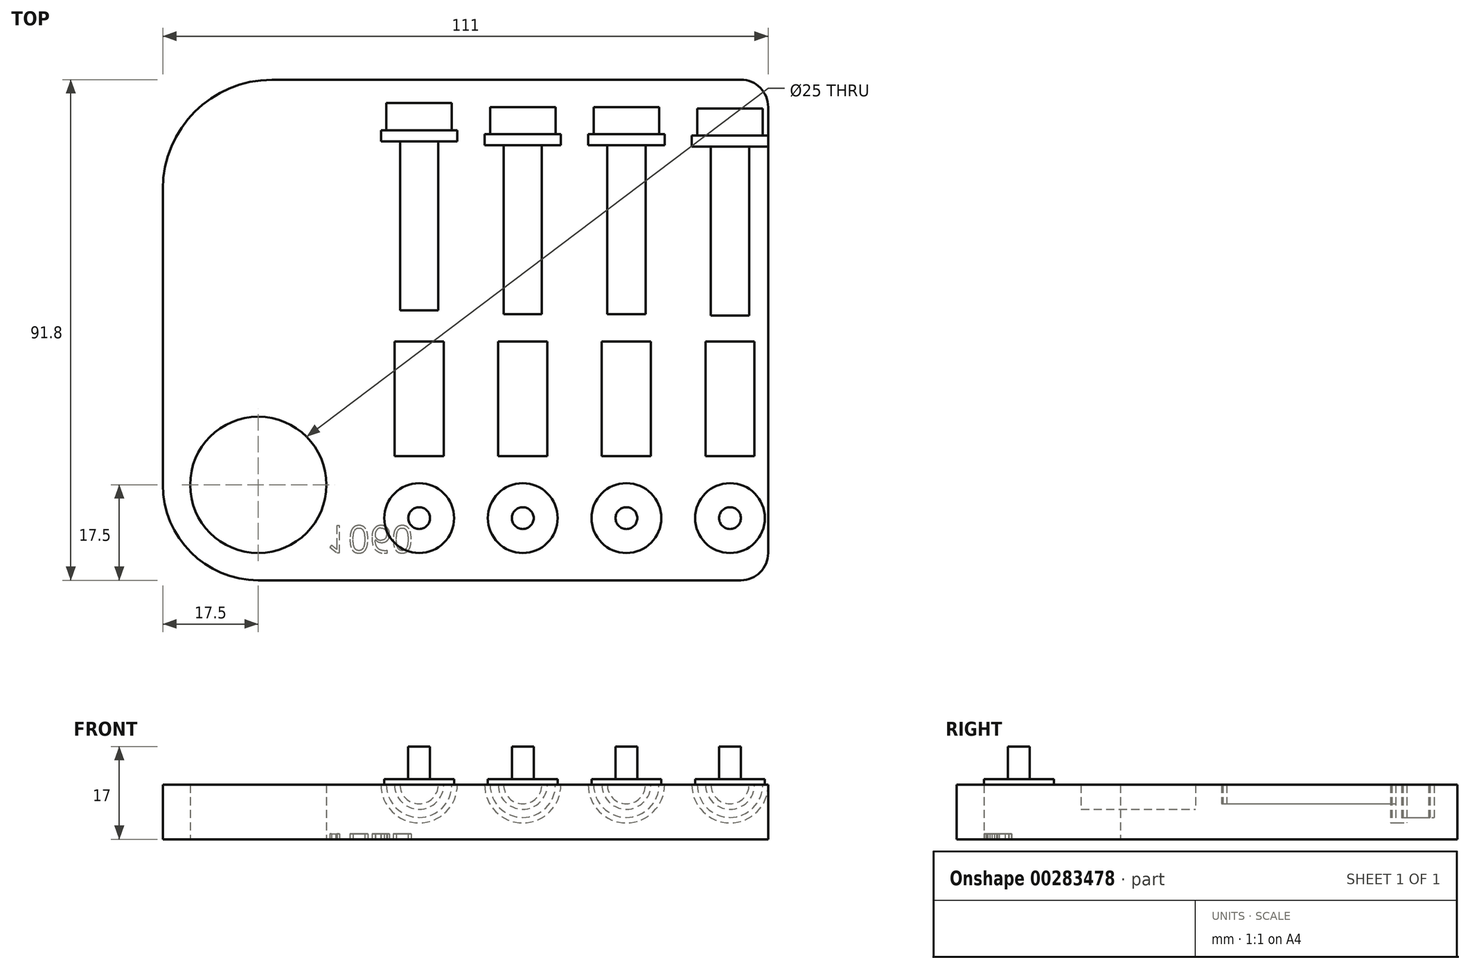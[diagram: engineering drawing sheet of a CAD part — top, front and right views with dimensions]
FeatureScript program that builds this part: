
annotation { "Feature Type Name" : "Feature", "Feature Type Description" : "" }
export const myFeature = defineFeature(function(context is Context, id is Id, definition is map)
    precondition{}
    {
        {
            var Q0;
            Q0=qCreatedBy(makeId("Top.planeOp"),FACE);
            var sketch = newSketch(context, id + "F0", { "sketchPlane" : qUnion([Q0])});
            skLineSegment(sketch, "E0.bottom", {"start": v(17.5, 0) * mm, "end": v(106, 0) * mm});
            skLineSegment(sketch, "E0.top", {"start": v(20, 91.8) * mm, "end": v(106, 91.8) * mm});
            skLineSegment(sketch, "E0.left", {"start": v(0, 17.5) * mm, "end": v(0, 71.8) * mm});
            skLineSegment(sketch, "E0.right", {"start": v(111, 5) * mm, "end": v(111, 86.8) * mm});
            skLineSegment(sketch, "E1.bottom", {"start": v(0, 0) * mm, "end": v(17.5, 0) * mm, "construction": true});
            skLineSegment(sketch, "E1.top", {"start": v(0, 17.5) * mm, "end": v(17.5, 17.5) * mm, "construction": true});
            skLineSegment(sketch, "E1.left", {"start": v(0, 0) * mm, "end": v(0, 17.5) * mm, "construction": true});
            skLineSegment(sketch, "E1.right", {"start": v(17.5, 0) * mm, "end": v(17.5, 17.5) * mm, "construction": true});
            skCircle(sketch, "E2", {"center": v(17.5, 17.5) * mm, "radius": 12.5 * mm});
            skPoint(sketch, "E3.visualSharp", {"position": v(0, 0) * mm});
            skArc(sketch, "E3.filletArc", {"start": v(0, 17.5) * mm, "mid": v(5.13, 5.13) * mm, "end": v(17.5, 0) * mm});
            skPoint(sketch, "E4.visualSharp", {"position": v(0, 91.8) * mm});
            skArc(sketch, "E4.filletArc", {"start": v(20, 91.8) * mm, "mid": v(5.86, 85.94) * mm, "end": v(0, 71.8) * mm});
            skPoint(sketch, "E5.visualSharp", {"position": v(111, 91.8) * mm});
            skArc(sketch, "E5.filletArc", {"start": v(111, 86.8) * mm, "mid": v(109.54, 90.34) * mm, "end": v(106, 91.8) * mm});
            skPoint(sketch, "E6.visualSharp", {"position": v(111, 0) * mm});
            skArc(sketch, "E6.filletArc", {"start": v(106, 0) * mm, "mid": v(109.54, 1.46) * mm, "end": v(111, 5) * mm});
            skSolve(sketch);
        }
        {
            var Q0;
            Q0=makeQuery(id+"F0.imprint","IMPRINT",FACE,{"disambiguationData":[TD([[makeQuery(id+"F0.imprint","IMPRINT",EDGE,{"derivedFrom":sQuery(id+"F0.wireOp",EDGE,"E0.bottom")}),1.0]])]});
            extrude(context, id + "F1", {"entities" : qUnion([Q0]), "depth" : 10 * mm});
        }
        {
            var Q0;
            Q0=makeQuery(id+"F1.opExtrude","CAP_FACE",FACE,{"disambiguationData":[OSD([sQuery(id+"F0.wireOp",EDGE,"E0.bottom"),sQuery(id+"F0.wireOp",EDGE,"E0.top"),sQuery(id+"F0.wireOp",EDGE,"E0.right"),sQuery(id+"F0.wireOp",EDGE,"E2"),sQuery(id+"F0.wireOp",EDGE,"E3.filletArc"),sQuery(id+"F0.wireOp",EDGE,"E4.filletArc"),sQuery(id+"F0.wireOp",EDGE,"E5.filletArc"),sQuery(id+"F0.wireOp",EDGE,"E6.filletArc")])],"isStart":false});
            var sketch = newSketch(context, id + "F2", { "sketchPlane" : qUnion([Q0])});
            skLineSegment(sketch, "E7.bottom", {"start": v(0, 0) * mm, "end": v(47, 0) * mm, "construction": true});
            skLineSegment(sketch, "E7.top", {"start": v(0, 11.4) * mm, "end": v(47, 11.4) * mm, "construction": true});
            skLineSegment(sketch, "E7.left", {"start": v(0, 0) * mm, "end": v(0, 11.4) * mm, "construction": true});
            skLineSegment(sketch, "E7.right", {"start": v(47, 0) * mm, "end": v(47, 11.4) * mm, "construction": true});
            skLineSegment(sketch, "E8.bottom", {"start": v(47, 11.4) * mm, "end": v(66, 11.4) * mm, "construction": true});
            skLineSegment(sketch, "E8.top", {"start": v(47, 22.8) * mm, "end": v(66, 22.8) * mm, "construction": true});
            skLineSegment(sketch, "E8.left", {"start": v(47, 11.4) * mm, "end": v(47, 22.8) * mm, "construction": true});
            skLineSegment(sketch, "E8.right", {"start": v(66, 11.4) * mm, "end": v(66, 22.8) * mm, "construction": true});
            skLineSegment(sketch, "E9.bottom", {"start": v(66, 11.4) * mm, "end": v(85, 11.4) * mm, "construction": true});
            skLineSegment(sketch, "E9.top", {"start": v(66, 22.8) * mm, "end": v(85, 22.8) * mm, "construction": true});
            skLineSegment(sketch, "E9.right", {"start": v(85, 11.4) * mm, "end": v(85, 22.8) * mm, "construction": true});
            skLineSegment(sketch, "E10.bottom", {"start": v(85, 11.4) * mm, "end": v(104, 11.4) * mm, "construction": true});
            skLineSegment(sketch, "E10.top", {"start": v(85, 22.8) * mm, "end": v(104, 22.8) * mm, "construction": true});
            skLineSegment(sketch, "E10.right", {"start": v(104, 11.4) * mm, "end": v(104, 22.8) * mm, "construction": true});
            skLineSegment(sketch, "E11.bottom", {"start": v(47, 22.8) * mm, "end": v(51.5, 22.8) * mm});
            skLineSegment(sketch, "E11.top", {"start": v(47, 43.8) * mm, "end": v(51.5, 43.8) * mm});
            skLineSegment(sketch, "E11.left", {"start": v(47, 22.8) * mm, "end": v(47, 43.8) * mm});
            skLineSegment(sketch, "E11.right", {"start": v(51.5, 22.8) * mm, "end": v(51.5, 43.8) * mm});
            skLineSegment(sketch, "E12.bottom", {"start": v(66, 22.8) * mm, "end": v(70.5, 22.8) * mm});
            skLineSegment(sketch, "E12.top", {"start": v(66, 43.8) * mm, "end": v(70.5, 43.8) * mm});
            skLineSegment(sketch, "E12.left", {"start": v(66, 22.8) * mm, "end": v(66, 43.8) * mm});
            skLineSegment(sketch, "E12.right", {"start": v(70.5, 22.8) * mm, "end": v(70.5, 43.8) * mm});
            skLineSegment(sketch, "E13.bottom", {"start": v(85, 22.8) * mm, "end": v(89.5, 22.8) * mm});
            skLineSegment(sketch, "E13.top", {"start": v(85, 43.8) * mm, "end": v(89.5, 43.8) * mm});
            skLineSegment(sketch, "E13.left", {"start": v(85, 22.8) * mm, "end": v(85, 43.8) * mm});
            skLineSegment(sketch, "E13.right", {"start": v(89.5, 22.8) * mm, "end": v(89.5, 43.8) * mm});
            skLineSegment(sketch, "E14.bottom", {"start": v(104, 22.8) * mm, "end": v(108.5, 22.8) * mm});
            skLineSegment(sketch, "E14.top", {"start": v(104, 43.8) * mm, "end": v(108.5, 43.8) * mm});
            skLineSegment(sketch, "E14.left", {"start": v(104, 22.8) * mm, "end": v(104, 43.8) * mm});
            skLineSegment(sketch, "E14.right", {"start": v(108.5, 22.8) * mm, "end": v(108.5, 43.8) * mm});
            skCircle(sketch, "E15", {"center": v(47, 11.4) * mm, "radius": 6.4 * mm});
            skCircle(sketch, "E16", {"center": v(66, 11.4) * mm, "radius": 6.4 * mm});
            skCircle(sketch, "E17", {"center": v(85, 11.4) * mm, "radius": 6.4 * mm});
            skCircle(sketch, "E18", {"center": v(104, 11.4) * mm, "radius": 6.4 * mm});
            skCircle(sketch, "E19", {"center": v(104, 11.4) * mm, "radius": 2 * mm});
            skCircle(sketch, "E20", {"center": v(85, 11.4) * mm, "radius": 2 * mm});
            skCircle(sketch, "E21", {"center": v(66, 11.4) * mm, "radius": 2 * mm});
            skCircle(sketch, "E22", {"center": v(47, 11.4) * mm, "radius": 2 * mm});
            skLineSegment(sketch, "E23", {"start": v(47, 43.8) * mm, "end": v(47, 48.8) * mm, "construction": true});
            skLineSegment(sketch, "E24", {"start": v(66, 43.8) * mm, "end": v(66, 48.8) * mm, "construction": true});
            skLineSegment(sketch, "E25", {"start": v(85, 43.8) * mm, "end": v(85, 48.8) * mm, "construction": true});
            skLineSegment(sketch, "E26", {"start": v(104, 43.8) * mm, "end": v(104, 48.55) * mm, "construction": true});
            skLineSegment(sketch, "E27.bottom", {"start": v(47, 49.52) * mm, "end": v(50.5, 49.52) * mm});
            skLineSegment(sketch, "E27.left", {"start": v(47, 49.52) * mm, "end": v(47, 80.52) * mm});
            skLineSegment(sketch, "E27.right", {"start": v(50.5, 49.52) * mm, "end": v(50.5, 80.52) * mm});
            skLineSegment(sketch, "E28.bottom", {"start": v(50.5, 80.52) * mm, "end": v(54, 80.52) * mm});
            skLineSegment(sketch, "E28.top", {"start": v(53, 82.52) * mm, "end": v(54, 82.52) * mm});
            skLineSegment(sketch, "E28.left", {"start": v(47, 80.52) * mm, "end": v(47, 82.52) * mm});
            skLineSegment(sketch, "E28.right", {"start": v(54, 80.52) * mm, "end": v(54, 82.52) * mm});
            skLineSegment(sketch, "E29.top", {"start": v(47, 87.52) * mm, "end": v(53, 87.52) * mm});
            skLineSegment(sketch, "E29.left", {"start": v(47, 82.52) * mm, "end": v(47, 87.52) * mm});
            skLineSegment(sketch, "E29.right", {"start": v(53, 82.52) * mm, "end": v(53, 87.52) * mm});
            skLineSegment(sketch, "E30.bottom", {"start": v(66, 48.8) * mm, "end": v(69.5, 48.8) * mm});
            skLineSegment(sketch, "E30.left", {"start": v(66, 48.8) * mm, "end": v(66, 79.8) * mm});
            skLineSegment(sketch, "E30.right", {"start": v(69.5, 48.8) * mm, "end": v(69.5, 79.8) * mm});
            skLineSegment(sketch, "E31.bottom", {"start": v(69.5, 79.8) * mm, "end": v(73, 79.8) * mm});
            skLineSegment(sketch, "E31.top", {"start": v(72, 81.8) * mm, "end": v(73, 81.8) * mm});
            skLineSegment(sketch, "E31.left", {"start": v(66, 79.8) * mm, "end": v(66, 81.8) * mm});
            skLineSegment(sketch, "E31.right", {"start": v(73, 79.8) * mm, "end": v(73, 81.8) * mm});
            skLineSegment(sketch, "E32.top", {"start": v(66, 86.8) * mm, "end": v(72, 86.8) * mm});
            skLineSegment(sketch, "E32.left", {"start": v(66, 81.8) * mm, "end": v(66, 86.8) * mm});
            skLineSegment(sketch, "E32.right", {"start": v(72, 81.8) * mm, "end": v(72, 86.8) * mm});
            skLineSegment(sketch, "E33.bottom", {"start": v(85, 48.8) * mm, "end": v(88.5, 48.8) * mm});
            skLineSegment(sketch, "E33.left", {"start": v(85, 48.8) * mm, "end": v(85, 79.8) * mm});
            skLineSegment(sketch, "E33.right", {"start": v(88.5, 48.8) * mm, "end": v(88.5, 79.8) * mm});
            skLineSegment(sketch, "E34.bottom", {"start": v(88.5, 79.8) * mm, "end": v(92, 79.8) * mm});
            skLineSegment(sketch, "E34.top", {"start": v(91, 81.8) * mm, "end": v(92, 81.8) * mm});
            skLineSegment(sketch, "E34.left", {"start": v(85, 79.8) * mm, "end": v(85, 81.8) * mm});
            skLineSegment(sketch, "E34.right", {"start": v(92, 79.8) * mm, "end": v(92, 81.8) * mm});
            skLineSegment(sketch, "E35.top", {"start": v(85, 86.8) * mm, "end": v(91, 86.8) * mm});
            skLineSegment(sketch, "E35.left", {"start": v(85, 81.8) * mm, "end": v(85, 86.8) * mm});
            skLineSegment(sketch, "E35.right", {"start": v(91, 81.8) * mm, "end": v(91, 86.8) * mm});
            skLineSegment(sketch, "E36.bottom", {"start": v(104, 48.55) * mm, "end": v(107.5, 48.55) * mm});
            skLineSegment(sketch, "E36.left", {"start": v(104, 48.55) * mm, "end": v(104, 79.55) * mm});
            skLineSegment(sketch, "E36.right", {"start": v(107.5, 48.55) * mm, "end": v(107.5, 79.55) * mm});
            skLineSegment(sketch, "E37.bottom", {"start": v(107.5, 79.55) * mm, "end": v(111, 79.55) * mm});
            skLineSegment(sketch, "E37.top", {"start": v(110, 81.55) * mm, "end": v(111, 81.55) * mm});
            skLineSegment(sketch, "E37.left", {"start": v(104, 79.55) * mm, "end": v(104, 81.55) * mm});
            skLineSegment(sketch, "E37.right", {"start": v(111, 79.55) * mm, "end": v(111, 81.55) * mm});
            skLineSegment(sketch, "E38.top", {"start": v(104, 86.55) * mm, "end": v(110, 86.55) * mm});
            skLineSegment(sketch, "E38.left", {"start": v(104, 81.55) * mm, "end": v(104, 86.55) * mm});
            skLineSegment(sketch, "E38.right", {"start": v(110, 81.55) * mm, "end": v(110, 86.55) * mm});
            skSolve(sketch);
        }
        {
            var Q0;
            Q0=makeQuery(id+"F2.imprint","IMPRINT",FACE,{"disambiguationData":[TD([[makeQuery(id+"F2.imprint","IMPRINT",EDGE,{"derivedFrom":sQuery(id+"F2.wireOp",EDGE,"E27.bottom")}),1.0]])]});
            var Q1;
            Q1=makeQuery(id+"F2.imprint","IMPRINT",FACE,{"disambiguationData":[TD([[makeQuery(id+"F2.imprint","IMPRINT",EDGE,{"derivedFrom":sQuery(id+"F2.wireOp",EDGE,"E11.bottom")}),1.0]])]});
            var Q2;
            Q2=sQuery(id+"F2.wireOp",EDGE,"E11.left");
            revolve(context, id + "F3", {"operationType" : NewBodyOperationType.REMOVE, "entities" : qUnion([Q0, Q1]), "axis" : qUnion([Q2]), "revolveType" : RevolveType.FULL, "oppositeDirection" : true});
        }
        {
            var Q0;
            Q0=makeQuery(id+"F2.imprint","IMPRINT",FACE,{"disambiguationData":[TD([[makeQuery(id+"F2.imprint","IMPRINT",EDGE,{"derivedFrom":sQuery(id+"F2.wireOp",EDGE,"E30.bottom")}),1.0]])]});
            var Q1;
            Q1=makeQuery(id+"F2.imprint","IMPRINT",FACE,{"disambiguationData":[TD([[makeQuery(id+"F2.imprint","IMPRINT",EDGE,{"derivedFrom":sQuery(id+"F2.wireOp",EDGE,"E12.bottom")}),1.0]])]});
            var Q2;
            Q2=sQuery(id+"F2.wireOp",EDGE,"E12.left");
            revolve(context, id + "F4", {"operationType" : NewBodyOperationType.REMOVE, "entities" : qUnion([Q0, Q1]), "axis" : qUnion([Q2]), "revolveType" : RevolveType.FULL, "oppositeDirection" : true});
        }
        {
            var Q0;
            Q0=makeQuery(id+"F2.imprint","IMPRINT",FACE,{"disambiguationData":[TD([[makeQuery(id+"F2.imprint","IMPRINT",EDGE,{"derivedFrom":sQuery(id+"F2.wireOp",EDGE,"E33.bottom")}),1.0]])]});
            var Q1;
            Q1=makeQuery(id+"F2.imprint","IMPRINT",FACE,{"disambiguationData":[TD([[makeQuery(id+"F2.imprint","IMPRINT",EDGE,{"derivedFrom":sQuery(id+"F2.wireOp",EDGE,"E13.bottom")}),1.0]])]});
            var Q2;
            Q2=sQuery(id+"F2.wireOp",EDGE,"E13.left");
            revolve(context, id + "F5", {"operationType" : NewBodyOperationType.REMOVE, "entities" : qUnion([Q0, Q1]), "axis" : qUnion([Q2]), "revolveType" : RevolveType.FULL, "oppositeDirection" : true});
        }
        {
            var Q0;
            Q0=makeQuery(id+"F2.imprint","IMPRINT",FACE,{"disambiguationData":[TD([[makeQuery(id+"F2.imprint","IMPRINT",EDGE,{"derivedFrom":sQuery(id+"F2.wireOp",EDGE,"E36.bottom")}),1.0]])]});
            var Q1;
            Q1=makeQuery(id+"F2.imprint","IMPRINT",FACE,{"disambiguationData":[TD([[makeQuery(id+"F2.imprint","IMPRINT",EDGE,{"derivedFrom":sQuery(id+"F2.wireOp",EDGE,"E14.bottom")}),1.0]])]});
            var Q2;
            Q2=sQuery(id+"F2.wireOp",EDGE,"E36.left");
            revolve(context, id + "F6", {"operationType" : NewBodyOperationType.REMOVE, "entities" : qUnion([Q0, Q1]), "axis" : qUnion([Q2]), "revolveType" : RevolveType.FULL, "oppositeDirection" : true});
        }
        {
            var Q0;
            Q0=makeQuery(id+"F2.imprint","IMPRINT",FACE,{"disambiguationData":[TD([[makeQuery(id+"F2.imprint","IMPRINT",EDGE,{"derivedFrom":sQuery(id+"F2.wireOp",EDGE,"E15")}),1.0]])]});
            var Q1;
            Q1=makeQuery(id+"F2.imprint","IMPRINT",FACE,{"disambiguationData":[TD([[makeQuery(id+"F2.imprint","IMPRINT",EDGE,{"derivedFrom":sQuery(id+"F2.wireOp",EDGE,"E16")}),1.0]])]});
            var Q2;
            Q2=makeQuery(id+"F2.imprint","IMPRINT",FACE,{"disambiguationData":[TD([[makeQuery(id+"F2.imprint","IMPRINT",EDGE,{"derivedFrom":sQuery(id+"F2.wireOp",EDGE,"E17")}),1.0]])]});
            var Q3;
            Q3=makeQuery(id+"F2.imprint","IMPRINT",FACE,{"disambiguationData":[TD([[makeQuery(id+"F2.imprint","IMPRINT",EDGE,{"derivedFrom":sQuery(id+"F2.wireOp",EDGE,"E18")}),1.0]])]});
            extrude(context, id + "F7", {"entities" : qUnion([Q0, Q1, Q2, Q3]), "operationType" : NewBodyOperationType.ADD, "depth" : 1 * mm});
        }
        {
            var Q0;
            Q0=makeQuery(id+"F2.imprint","IMPRINT",FACE,{"disambiguationData":[TD([[makeQuery(id+"F2.imprint","IMPRINT",EDGE,{"derivedFrom":sQuery(id+"F2.wireOp",EDGE,"E21")}),1.0]])]});
            var Q1;
            Q1=makeQuery(id+"F2.imprint","IMPRINT",FACE,{"disambiguationData":[TD([[makeQuery(id+"F2.imprint","IMPRINT",EDGE,{"derivedFrom":sQuery(id+"F2.wireOp",EDGE,"E22")}),1.0]])]});
            var Q2;
            Q2=makeQuery(id+"F2.imprint","IMPRINT",FACE,{"disambiguationData":[TD([[makeQuery(id+"F2.imprint","IMPRINT",EDGE,{"derivedFrom":sQuery(id+"F2.wireOp",EDGE,"E20")}),1.0]])]});
            var Q3;
            Q3=makeQuery(id+"F2.imprint","IMPRINT",FACE,{"disambiguationData":[TD([[makeQuery(id+"F2.imprint","IMPRINT",EDGE,{"derivedFrom":sQuery(id+"F2.wireOp",EDGE,"E19")}),1.0]])]});
            extrude(context, id + "F8", {"entities" : qUnion([Q0, Q1, Q2, Q3]), "operationType" : NewBodyOperationType.ADD, "depth" : 7 * mm});
        }
        {
            var Q0;
            Q0=makeQuery(id+"F1.opExtrude","CAP_FACE",FACE,{"disambiguationData":[OSD([sQuery(id+"F0.wireOp",EDGE,"E0.bottom"),sQuery(id+"F0.wireOp",EDGE,"E0.top"),sQuery(id+"F0.wireOp",EDGE,"E0.left"),sQuery(id+"F0.wireOp",EDGE,"E0.right"),sQuery(id+"F0.wireOp",EDGE,"E2"),sQuery(id+"F0.wireOp",EDGE,"E3.filletArc"),sQuery(id+"F0.wireOp",EDGE,"E4.filletArc"),sQuery(id+"F0.wireOp",EDGE,"E5.filletArc"),sQuery(id+"F0.wireOp",EDGE,"E6.filletArc")])],"isStart":true});
            var sketch = newSketch(context, id + "F9", { "sketchPlane" : qUnion([Q0])});
            skLineSegment(sketch, "E39.bottom", {"start": v(0, 0) * mm, "end": v(30, 0) * mm, "construction": true});
            skLineSegment(sketch, "E39.top", {"start": v(0, -5) * mm, "end": v(30, -5) * mm, "construction": true});
            skLineSegment(sketch, "E39.left", {"start": v(0, 0) * mm, "end": v(0, -5) * mm, "construction": true});
            skLineSegment(sketch, "E39.right", {"start": v(30, 0) * mm, "end": v(30, -5) * mm, "construction": true});
            skText(sketch, "E40", { "text": "1060", "fontName": "OpenSans-Regular.ttf"});
            const initialGuessF9  = {"E40": [0.03, -0.01, 1, 0, 0.005]};
            skSetInitialGuess(sketch, initialGuessF9);
            skSolve(sketch);
        }
        {
            var Q0;
            Q0 = qSketchRegion(id + "F9", true);
            extrude(context, id + "F10", {"entities" : qUnion([Q0]), "operationType" : NewBodyOperationType.REMOVE, "oppositeDirection" : true, "depth" : 1 * mm});
        }
    });
